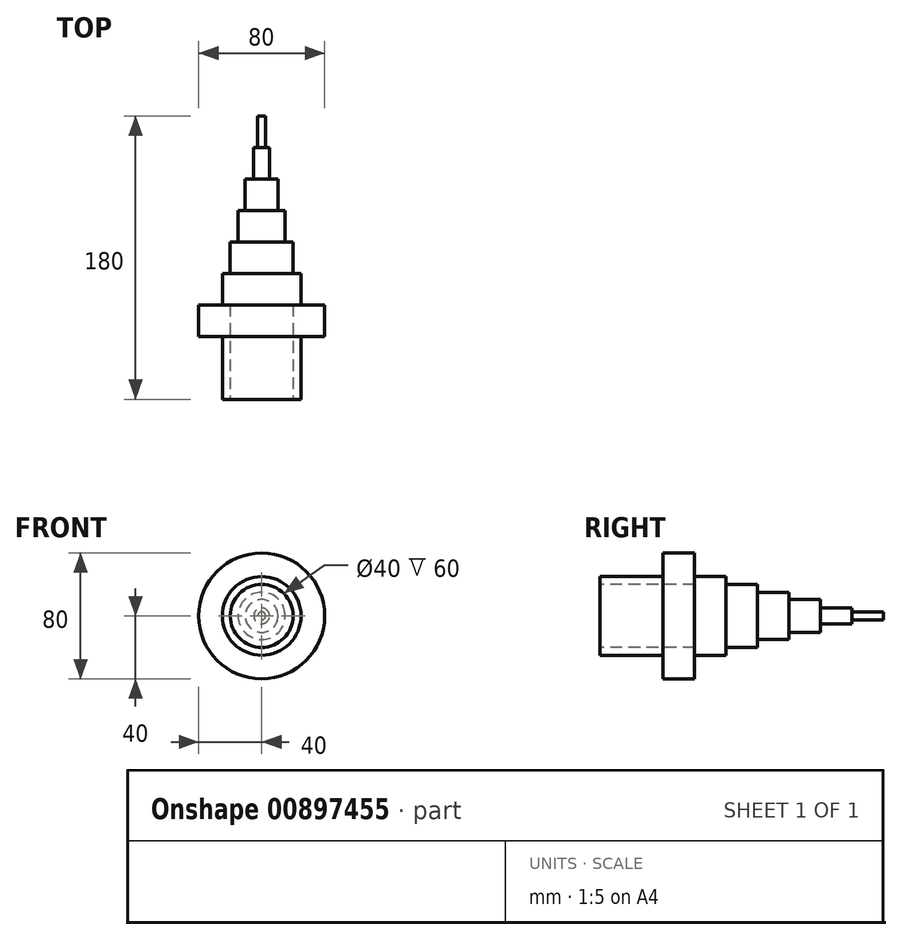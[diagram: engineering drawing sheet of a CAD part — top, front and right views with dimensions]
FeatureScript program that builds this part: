
annotation { "Feature Type Name" : "Feature", "Feature Type Description" : "" }
export const myFeature = defineFeature(function(context is Context, id is Id, definition is map)
    precondition{}
    {
        {
            var Q0;
            Q0=qCreatedBy(makeId("Front.planeOp"),FACE);
            var sketch = newSketch(context, id + "F0", { "sketchPlane" : qUnion([Q0])});
            skCircle(sketch, "E0", {"center": v(0, 0) * mm, "radius": 40 * mm});
            skSolve(sketch);
        }
        {
            var Q0;
            Q0=makeQuery(id+"F0.imprint","IMPRINT",FACE,{"disambiguationData":[TD([[makeQuery(id+"F0.imprint","IMPRINT",EDGE,{"derivedFrom":sQuery(id+"F0.wireOp",EDGE,"E0")}),1.0]])]});
            extrude(context, id + "F1", {"entities" : qUnion([Q0]), "depth" : 20 * mm, "offsetDistance" : 25.4 * mm});
        }
        {
            var Q0;
            Q0=makeQuery(id+"F1.opExtrude","CAP_FACE",FACE,{"disambiguationData":[OSD([sQuery(id+"F0.wireOp",EDGE,"E0")])],"isStart":true});
            var sketch = newSketch(context, id + "F2", { "sketchPlane" : qUnion([Q0])});
            skCircle(sketch, "E1", {"center": v(0, 0) * mm, "radius": 25 * mm});
            skSolve(sketch);
        }
        {
            var Q0;
            Q0 = qSketchRegion(id + "F2", true);
            extrude(context, id + "F3", {"entities" : qUnion([Q0]), "operationType" : NewBodyOperationType.ADD, "depth" : 20 * mm, "offsetDistance" : 25.4 * mm});
        }
        {
            var Q0;
            Q0=makeQuery(id+"F3.opExtrude","CAP_FACE",FACE,{"disambiguationData":[OSD([sQuery(id+"F2.wireOp",EDGE,"E1")])],"isStart":false});
            var sketch = newSketch(context, id + "F4", { "sketchPlane" : qUnion([Q0])});
            skCircle(sketch, "E2", {"center": v(0, 0) * mm, "radius": 20 * mm});
            skSolve(sketch);
        }
        {
            var Q0;
            Q0 = qSketchRegion(id + "F4", true);
            extrude(context, id + "F5", {"entities" : qUnion([Q0]), "operationType" : NewBodyOperationType.ADD, "depth" : 20 * mm, "offsetDistance" : 25.4 * mm});
        }
        {
            var Q0;
            Q0=makeQuery(id+"F5.opExtrude","CAP_FACE",FACE,{"disambiguationData":[OSD([sQuery(id+"F4.wireOp",EDGE,"E2")])],"isStart":false});
            var sketch = newSketch(context, id + "F6", { "sketchPlane" : qUnion([Q0])});
            skCircle(sketch, "E3", {"center": v(0, 0) * mm, "radius": 15 * mm});
            skSolve(sketch);
        }
        {
            var Q0;
            Q0 = qSketchRegion(id + "F6", true);
            extrude(context, id + "F7", {"entities" : qUnion([Q0]), "operationType" : NewBodyOperationType.ADD, "depth" : 20 * mm, "offsetDistance" : 25.4 * mm});
        }
        {
            var Q0;
            Q0=makeQuery(id+"F7.opExtrude","CAP_FACE",FACE,{"disambiguationData":[OSD([sQuery(id+"F6.wireOp",EDGE,"E3")])],"isStart":false});
            var sketch = newSketch(context, id + "F8", { "sketchPlane" : qUnion([Q0])});
            skCircle(sketch, "E4", {"center": v(0, 0) * mm, "radius": 10.42 * mm});
            skSolve(sketch);
        }
        {
            var Q0;
            Q0 = qSketchRegion(id + "F8", true);
            extrude(context, id + "F9", {"entities" : qUnion([Q0]), "operationType" : NewBodyOperationType.ADD, "depth" : 20 * mm, "offsetDistance" : 25.4 * mm});
        }
        {
            var Q0;
            Q0=makeQuery(id+"F9.opExtrude","CAP_FACE",FACE,{"disambiguationData":[OSD([sQuery(id+"F8.wireOp",EDGE,"E4")])],"isStart":false});
            var sketch = newSketch(context, id + "F10", { "sketchPlane" : qUnion([Q0])});
            skCircle(sketch, "E5", {"center": v(0, 0) * mm, "radius": 5 * mm});
            skSolve(sketch);
        }
        {
            var Q0;
            Q0 = qSketchRegion(id + "F10", true);
            extrude(context, id + "F11", {"entities" : qUnion([Q0]), "operationType" : NewBodyOperationType.ADD, "depth" : 20 * mm, "offsetDistance" : 25.4 * mm});
        }
        {
            var Q0;
            Q0=makeQuery(id+"F11.opExtrude","CAP_FACE",FACE,{"disambiguationData":[OSD([sQuery(id+"F10.wireOp",EDGE,"E5")])],"isStart":false});
            var sketch = newSketch(context, id + "F12", { "sketchPlane" : qUnion([Q0])});
            skCircle(sketch, "E6", {"center": v(0, 0) * mm, "radius": 2.5 * mm});
            skSolve(sketch);
        }
        {
            var Q0;
            Q0 = qSketchRegion(id + "F12", true);
            extrude(context, id + "F13", {"entities" : qUnion([Q0]), "operationType" : NewBodyOperationType.ADD, "depth" : 20 * mm, "offsetDistance" : 25.4 * mm});
        }
        {
            var Q0;
            Q0=makeQuery(id+"F1.opExtrude","CAP_FACE",FACE,{"disambiguationData":[OSD([sQuery(id+"F0.wireOp",EDGE,"E0")])],"isStart":false});
            var sketch = newSketch(context, id + "F14", { "sketchPlane" : qUnion([Q0])});
            skCircle(sketch, "E7", {"center": v(0, 0) * mm, "radius": 25 * mm});
            skSolve(sketch);
        }
        {
            var Q0;
            Q0 = qSketchRegion(id + "F14", true);
            extrude(context, id + "F15", {"entities" : qUnion([Q0]), "operationType" : NewBodyOperationType.ADD, "depth" : 40 * mm, "offsetDistance" : 25.4 * mm});
        }
        {
            var Q0;
            Q0=makeQuery(id+"F15.opExtrude","CAP_FACE",FACE,{"disambiguationData":[OSD([sQuery(id+"F14.wireOp",EDGE,"E7")])],"isStart":false});
            var sketch = newSketch(context, id + "F16", { "sketchPlane" : qUnion([Q0])});
            skCircle(sketch, "E8", {"center": v(0, 0) * mm, "radius": 20 * mm});
            skSolve(sketch);
        }
        {
            var Q0;
            Q0 = qSketchRegion(id + "F16", true);
            extrude(context, id + "F17", {"entities" : qUnion([Q0]), "operationType" : NewBodyOperationType.REMOVE, "oppositeDirection" : true, "depth" : 60 * mm, "offsetDistance" : 25.4 * mm});
        }
    });
